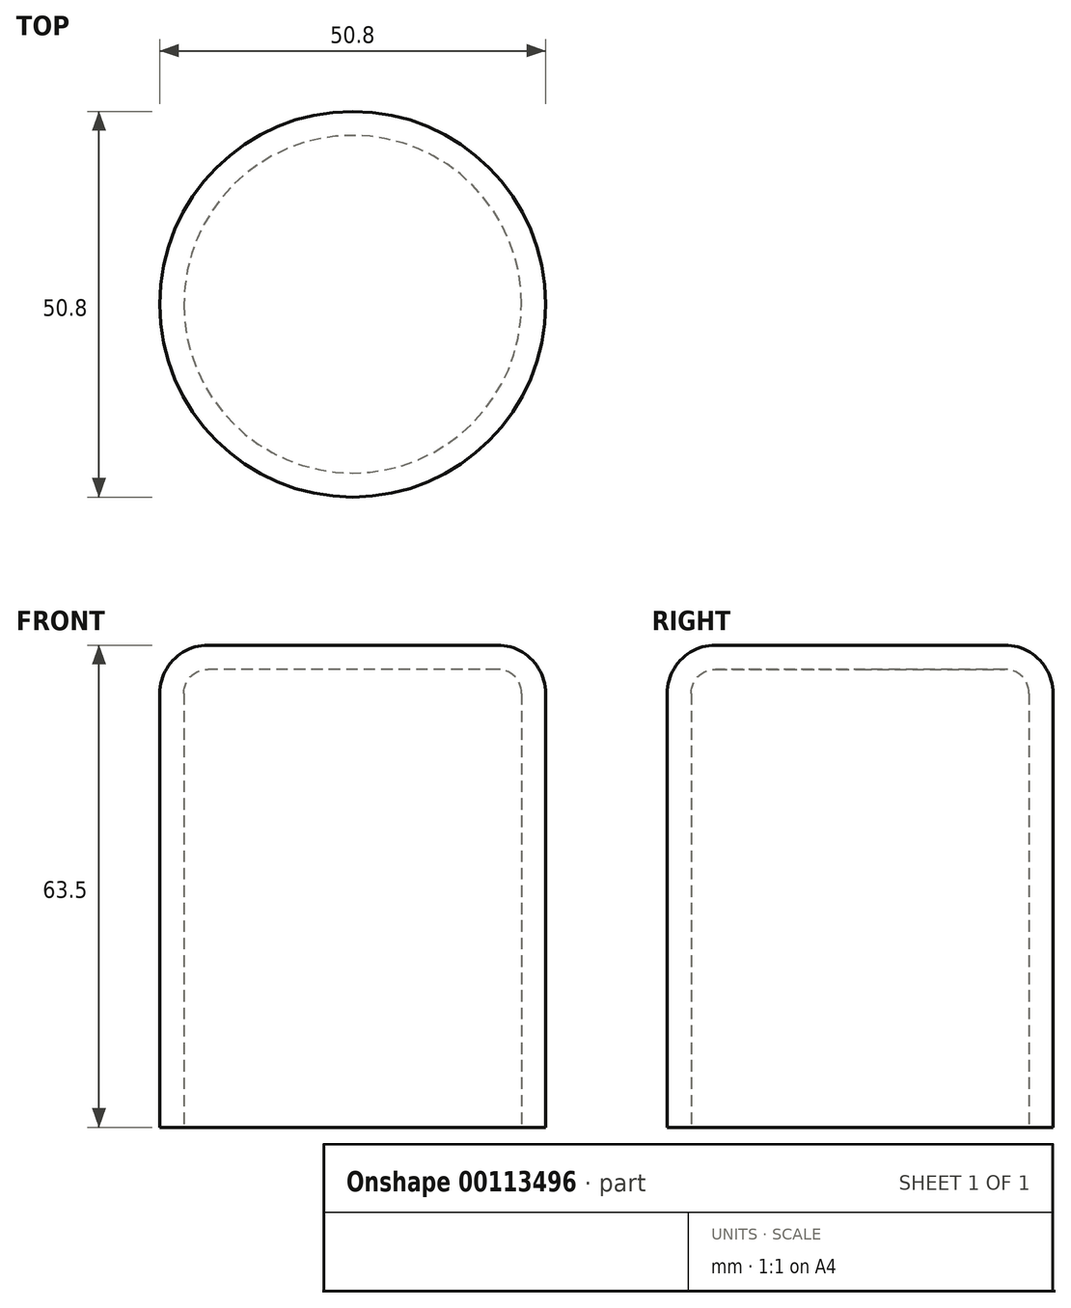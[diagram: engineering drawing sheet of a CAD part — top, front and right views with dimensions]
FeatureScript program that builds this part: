
annotation { "Feature Type Name" : "Feature", "Feature Type Description" : "" }
export const myFeature = defineFeature(function(context is Context, id is Id, definition is map)
    precondition{}
    {
        {
            var Q0;
            Q0=qCreatedBy(makeId("Top.planeOp"),FACE);
            var sketch = newSketch(context, id + "F0", { "sketchPlane" : qUnion([Q0])});
            skCircle(sketch, "E0", {"center": v(0, 0) * mm, "radius": 25.4 * mm});
            skSolve(sketch);
        }
        {
            var Q0;
            Q0 = qSketchRegion(id + "F0", true);
            extrude(context, id + "F1", {"entities" : qUnion([Q0]), "depth" : 63.5 * mm});
        }
        {
            var Q0;
            Q0=makeQuery(id+"F1.opExtrude","CAP_EDGE",EDGE,{"disambiguationData":[OSD([sQuery(id+"F0.wireOp",EDGE,"E0")])],"isStart":false});
            fillet(context, id + "F2", {"entities" : qUnion([Q0]), "radius" : 6.35 * mm, "tangentPropagation" : true, "allowEdgeOverflow" : false});
        }
        {
            var Q0;
            Q0=makeQuery(id+"F1.opExtrude","CAP_FACE",FACE,{"disambiguationData":[OSD([sQuery(id+"F0.wireOp",EDGE,"E0")])],"isStart":true});
            shell(context, id + "F3", {"entities" : qUnion([Q0]), "thickness" : 3.17 * mm});
        }
    });
